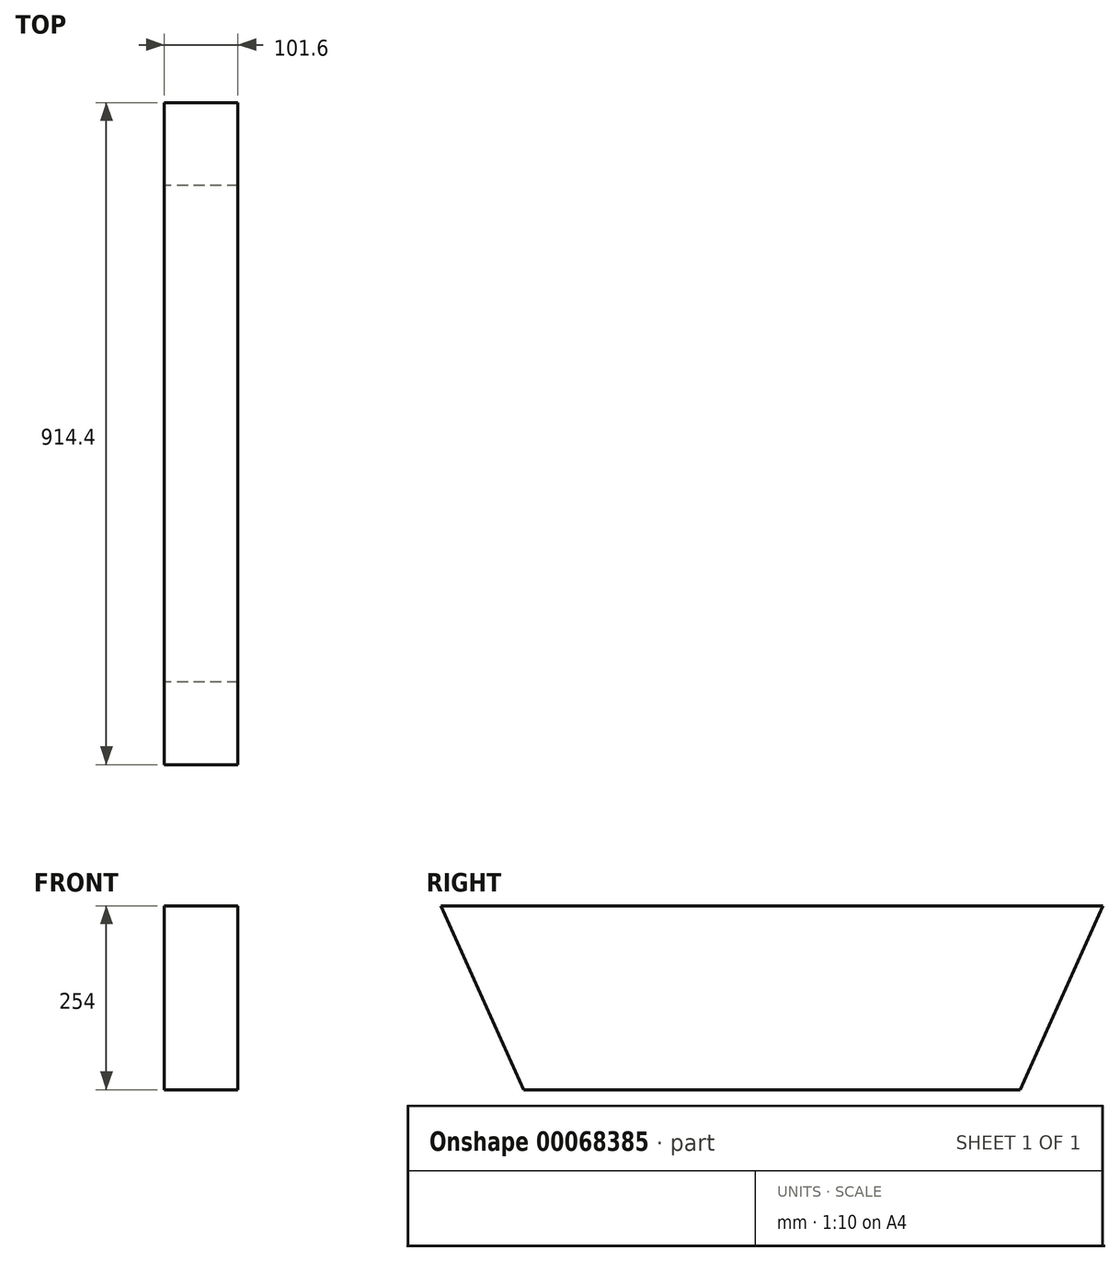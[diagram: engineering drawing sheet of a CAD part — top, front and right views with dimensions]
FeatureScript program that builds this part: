
annotation { "Feature Type Name" : "Feature", "Feature Type Description" : "" }
export const myFeature = defineFeature(function(context is Context, id is Id, definition is map)
    precondition{}
    {
        {
            var Q0;
            Q0=qCreatedBy(makeId("Right.planeOp"),FACE);
            var sketch = newSketch(context, id + "F0", { "sketchPlane" : qUnion([Q0])});
            skLineSegment(sketch, "E0.rect.bottom", {"start": v(342.9, 63.5) * mm, "end": v(-342.9, 63.5) * mm});
            skLineSegment(sketch, "E0.rect.top", {"start": v(342.9, -63.5) * mm, "end": v(-342.9, -63.5) * mm});
            skLineSegment(sketch, "E0.rect.left", {"start": v(342.9, 63.5) * mm, "end": v(342.9, -63.5) * mm});
            skLineSegment(sketch, "E0.rect.right", {"start": v(-342.9, 63.5) * mm, "end": v(-342.9, -63.5) * mm});
            skPoint(sketch, "E0.rect.middle", {"position": v(0, 0) * mm});
            skLineSegment(sketch, "E1", {"start": v(342.9, 63.5) * mm, "end": v(457.2, 63.5) * mm, "construction": true});
            skLineSegment(sketch, "E2", {"start": v(-342.9, 63.5) * mm, "end": v(-457.2, 63.5) * mm, "construction": true});
            skLineSegment(sketch, "E3.bottom", {"start": v(457.2, 63.5) * mm, "end": v(-457.2, 63.5) * mm});
            skLineSegment(sketch, "E3.top", {"start": v(457.2, 190.5) * mm, "end": v(-457.2, 190.5) * mm});
            skLineSegment(sketch, "E3.left", {"start": v(457.2, 63.5) * mm, "end": v(457.2, 190.5) * mm});
            skLineSegment(sketch, "E3.right", {"start": v(-457.2, 63.5) * mm, "end": v(-457.2, 190.5) * mm});
            skLineSegment(sketch, "E4", {"start": v(457.2, 190.5) * mm, "end": v(342.9, -63.5) * mm});
            skLineSegment(sketch, "E5", {"start": v(-342.9, -63.5) * mm, "end": v(-457.2, 190.5) * mm});
            skSolve(sketch);
        }
        {
            var Q0;
            {var subQ0=sQuery(id+"F0.wireOp",EDGE,"E0.rect.left");Q0=makeQuery(id+"F0.imprint","IMPRINT",FACE,{"disambiguationData":[TD([[makeQuery(id+"F0.imprint","IMPRINT",EDGE,{"derivedFrom":subQ0}),1.0]])]});}
            var Q1;
            {var subQ0=sQuery(id+"F0.wireOp",EDGE,"E0.rect.right");Q1=makeQuery(id+"F0.imprint","IMPRINT",FACE,{"disambiguationData":[TD([[makeQuery(id+"F0.imprint","IMPRINT",EDGE,{"derivedFrom":subQ0}),-1.0]])]});}
            var Q2;
            Q2=makeQuery(id+"F0.imprint","IMPRINT",FACE,{"disambiguationData":[TD([[makeQuery(id+"F0.imprint","IMPRINT",EDGE,{"derivedFrom":sQuery(id+"F0.wireOp",EDGE,"E0.rect.top")}),-1.0]])]});
            var Q3;
            {var subQ0=sQuery(id+"F0.wireOp",EDGE,"E3.top");Q3=makeQuery(id+"F0.imprint","IMPRINT",FACE,{"disambiguationData":[TD([[makeQuery(id+"F0.imprint","IMPRINT",EDGE,{"derivedFrom":subQ0}),1.0]])]});}
            extrude(context, id + "F1", {"entities" : qUnion([Q0, Q1, Q2, Q3]), "depth" : 101.6 * mm});
        }
    });
